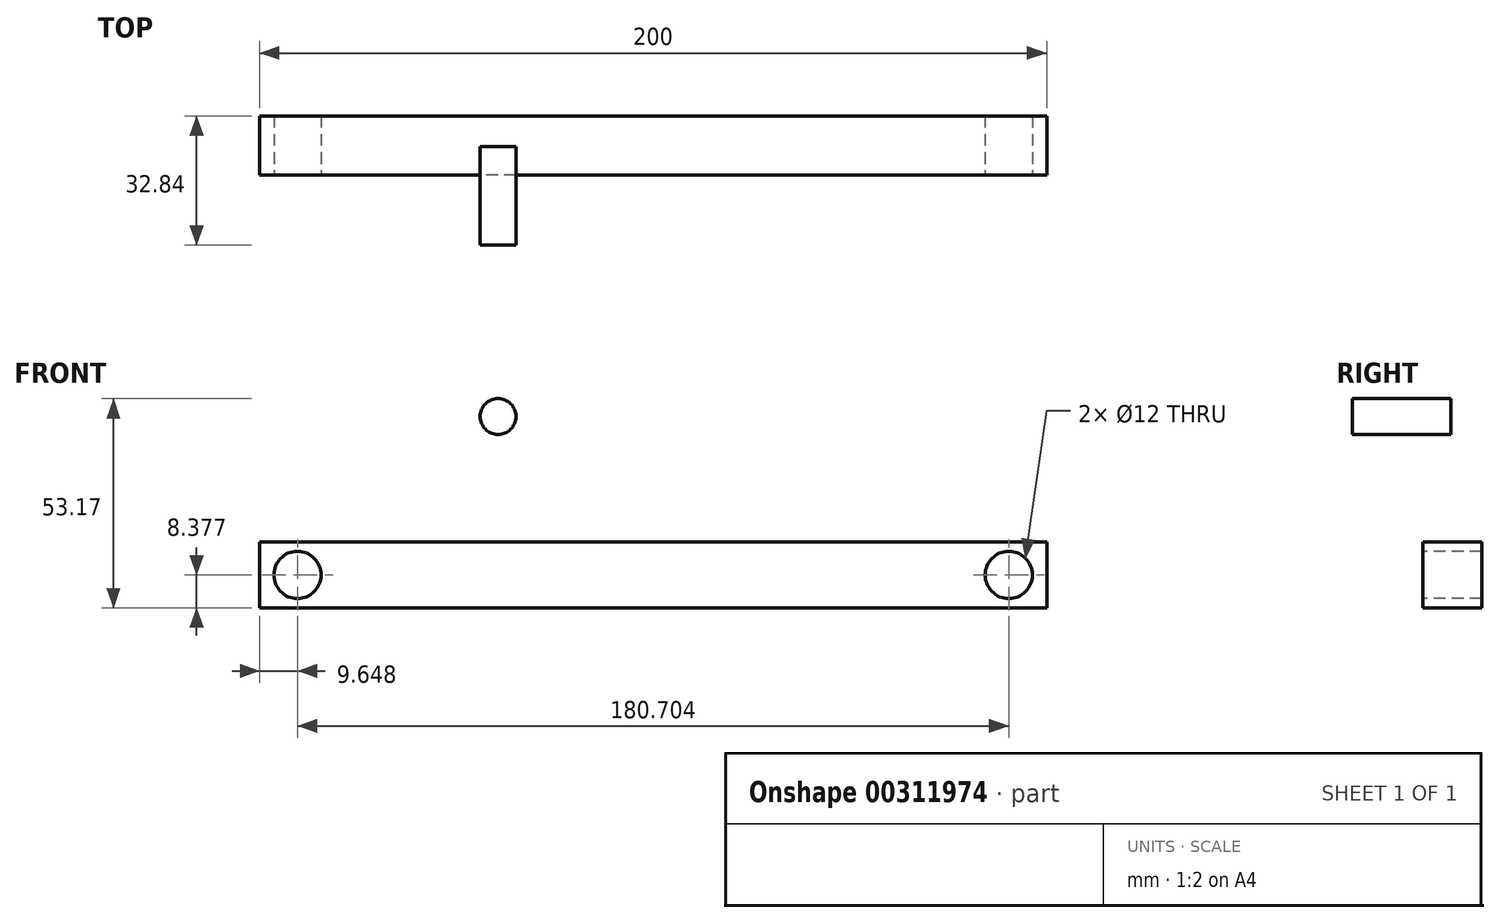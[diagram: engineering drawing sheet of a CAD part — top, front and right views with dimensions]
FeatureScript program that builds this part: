
annotation { "Feature Type Name" : "Feature", "Feature Type Description" : "" }
export const myFeature = defineFeature(function(context is Context, id is Id, definition is map)
    precondition{}
    {
        {
            var Q0;
            Q0=qCreatedBy(makeId("Right.planeOp"),FACE);
            var sketch = newSketch(context, id + "F0", { "sketchPlane" : qUnion([Q0])});
            skLineSegment(sketch, "E0.bottom", {"start": v(-7.16, 9.8) * mm, "end": v(7.84, 9.8) * mm});
            skLineSegment(sketch, "E0.top", {"start": v(-7.16, -6.96) * mm, "end": v(7.84, -6.96) * mm});
            skLineSegment(sketch, "E0.left", {"start": v(-7.16, 9.8) * mm, "end": v(-7.16, -6.96) * mm});
            skLineSegment(sketch, "E0.right", {"start": v(7.84, 9.8) * mm, "end": v(7.84, -6.96) * mm});
            skSolve(sketch);
        }
        {
            var Q0;
            Q0=makeQuery(id+"F0.imprint","IMPRINT",FACE,{"disambiguationData":[TD([[makeQuery(id+"F0.imprint","IMPRINT",EDGE,{"derivedFrom":sQuery(id+"F0.wireOp",EDGE,"E0.bottom")}),-1.0]])]});
            extrude(context, id + "F1", {"entities" : qUnion([Q0]), "endBound" : BoundingType.SYMMETRIC, "depth" : 200 * mm, "offsetDistance" : 25 * mm});
        }
        {
            var Q0;
            Q0=makeQuery(id+"F1.opExtrude","SWEPT_FACE",FACE,{"disambiguationData":[OSD([sQuery(id+"F0.wireOp",EDGE,"E0.left")])]});
            var sketch = newSketch(context, id + "F2", { "sketchPlane" : qUnion([Q0])});
            skPoint(sketch, "E1", {"position": v(90.35, 1.42) * mm});
            skLineSegment(sketch, "E2", {"start": v(90.35, 9.8) * mm, "end": v(90.35, -6.96) * mm, "construction": true});
            skPoint(sketch, "E3.MirrorP", {"position": v(-90.35, 1.42) * mm});
            skLineSegment(sketch, "E4.MirrorCS", {"start": v(-90.35, 9.8) * mm, "end": v(-90.35, -6.96) * mm, "construction": true});
            skSolve(sketch);
        }
        {
            var Q0;
            Q0=sQuery(id+"F2.wireOp",VERTEX,"E1");
            var Q1;
            Q1=sQuery(id+"F2.wireOp",VERTEX,"E3.MirrorP");
            var Q2;
            Q2=makeQuery(id+"F1.opExtrude","SWEPT_BODY",BODY,{"disambiguationData":[OSD([sQuery(id+"F0.wireOp",EDGE,"E0.bottom"),sQuery(id+"F0.wireOp",EDGE,"E0.top"),sQuery(id+"F0.wireOp",EDGE,"E0.left"),sQuery(id+"F0.wireOp",EDGE,"E0.right")])]});
            hole(context, id + "F3", {"style" : HoleStyle.SIMPLE, "endStyle" : HoleEndStyle.THROUGH, "holeDiameter" : 12 * mm, "majorDiameter" : 5 * mm, "isTappedThrough" : true, "tappedDepth" : 12 * mm, "tapClearance" : 3, "locations" : qUnion([Q0, Q1]), "scope" : qUnion([Q2])});
        }
        {
            var Q0;
            Q0=qCreatedBy(makeId("Front.planeOp"),FACE);
            var sketch = newSketch(context, id + "F4", { "sketchPlane" : qUnion([Q0])});
            skCircle(sketch, "E5", {"center": v(-39.4, 41.66) * mm, "radius": 4.54 * mm});
            skSolve(sketch);
        }
        {
            var Q0;
            Q0=makeQuery(id+"F4.imprint","IMPRINT",FACE,{"disambiguationData":[TD([[makeQuery(id+"F4.imprint","IMPRINT",EDGE,{"derivedFrom":sQuery(id+"F4.wireOp",EDGE,"E5")}),1.0]])]});
            extrude(context, id + "F5", {"entities" : qUnion([Q0]), "depth" : 25 * mm, "offsetDistance" : 25 * mm});
        }
    });
